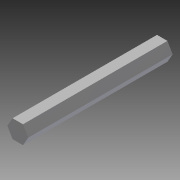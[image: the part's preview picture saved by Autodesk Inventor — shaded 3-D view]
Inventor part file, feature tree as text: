
AUTODESK INVENTOR PART (.ipt)
format: ipt  version: 2014 (Build 180170000, 170)  size: 84,992 bytes
history: native  units: in
note: dims shown in document units (in); Inventor stores cm internally (conversion verified against a paired STEP export)
features: extrude x1, sketch x1
ambient origin geometry x8: Origin, YZ Plane, XZ Plane, XY Plane, X Axis, Y Axis, Z Axis, Center Point
bodies: Solid1 (feature_tree)
feature tree (2):
  extrude  "Extrusion1"  Depth=4.0in TaperAngle=0.0deg
  sketch  "Sketch1"  dims[d0=0.5in d1=4.0in d2=0.0in]
